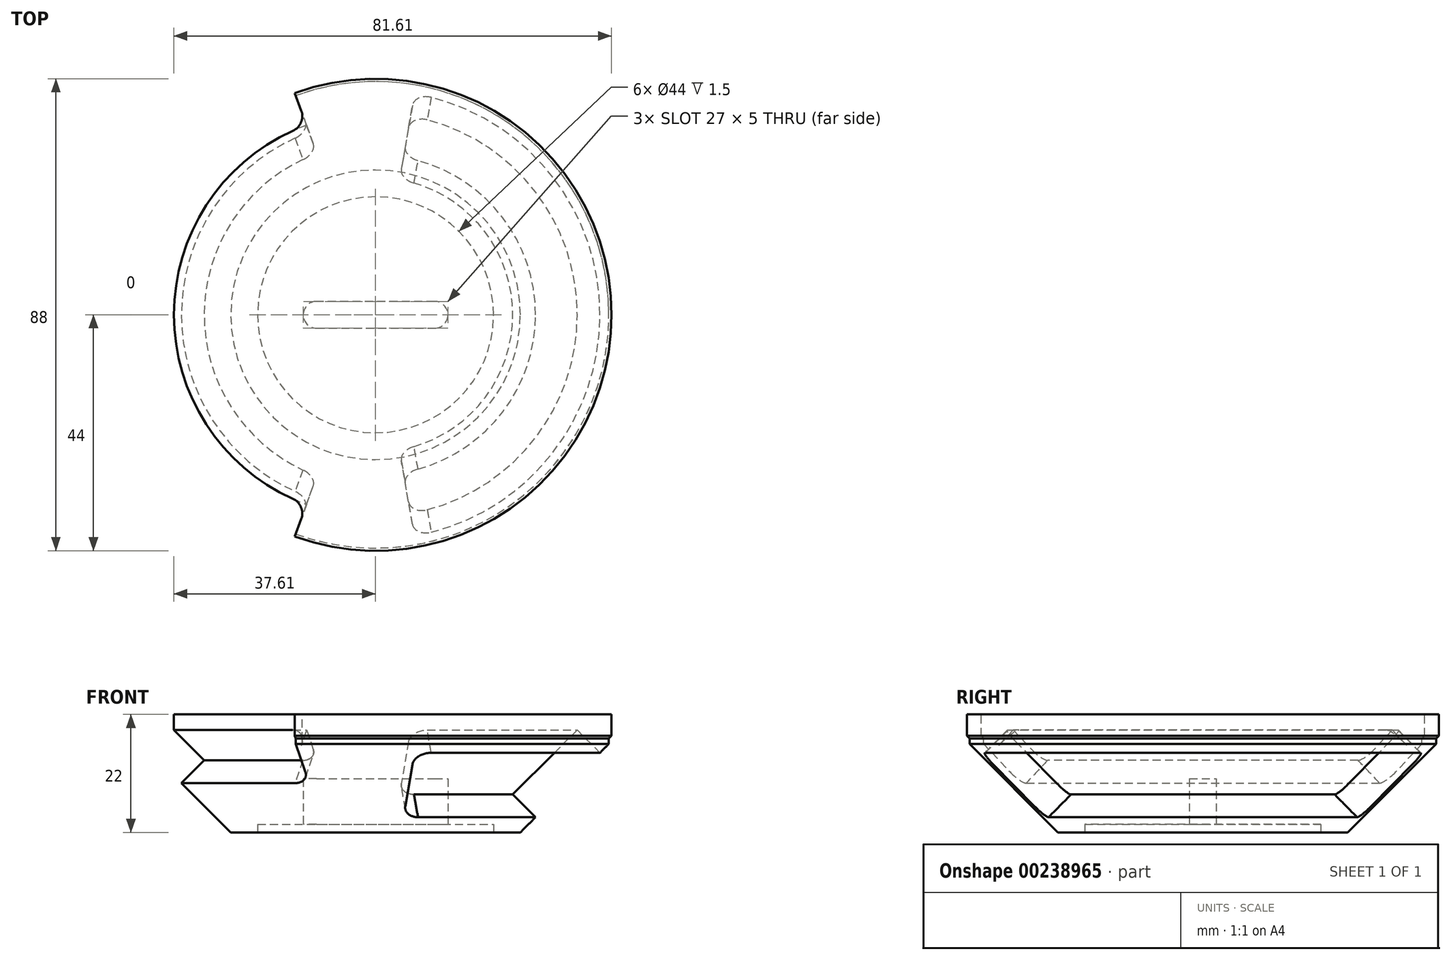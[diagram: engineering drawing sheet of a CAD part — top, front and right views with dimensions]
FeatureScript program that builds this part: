
annotation { "Feature Type Name" : "Feature", "Feature Type Description" : "" }
export const myFeature = defineFeature(function(context is Context, id is Id, definition is map)
    precondition{}
    {
        {
            var Q0;
            Q0=qCreatedBy(makeId("Front.planeOp"),FACE);
            var sketch = newSketch(context, id + "F0", { "sketchPlane" : qUnion([Q0])});
            skLineSegment(sketch, "E0", {"start": v(0, 70.12) * mm, "end": v(0, -51.14) * mm, "construction": true});
            skLineSegment(sketch, "E1", {"start": v(-27, -2) * mm, "end": v(-43.5, 14.5) * mm});
            skLineSegment(sketch, "E2", {"start": v(-44, 20) * mm, "end": v(0, 20) * mm});
            skLineSegment(sketch, "E3", {"start": v(0, 20) * mm, "end": v(0, -2) * mm});
            skLineSegment(sketch, "E4.trimOffspring", {"start": v(-27, -2) * mm, "end": v(0, -2) * mm});
            skLineSegment(sketch, "E5", {"start": v(-47.02, 16) * mm, "end": v(-44, 16) * mm});
            skLineSegment(sketch, "E6", {"start": v(-43.5, 15.5) * mm, "end": v(-43.5, 14.5) * mm});
            skLineSegment(sketch, "E7", {"start": v(-44, 16) * mm, "end": v(-43.5, 15.5) * mm});
            skLineSegment(sketch, "E8.trimOffspring", {"start": v(-44, 16) * mm, "end": v(-44, 20) * mm});
            skPoint(sketch, "E9.orphan", {"position": v(-44, 15) * mm});
            skSolve(sketch);
        }
        {
            var Q0;
            {var subQ0=sQuery(id+"F0.wireOp",EDGE,"E1");Q0=makeQuery(id+"F0.imprint","IMPRINT",FACE,{"disambiguationData":[TD([[makeQuery(id+"F0.imprint","IMPRINT",EDGE,{"derivedFrom":subQ0}),-1.0]])]});}
            var Q1;
            Q1=sQuery(id+"F0.wireOp",EDGE,"E0");
            revolve(context, id + "F1", {"entities" : qUnion([Q0]), "axis" : qUnion([Q1]), "revolveType" : RevolveType.FULL});
        }
        {
            var Q0;
            Q0=qCreatedBy(makeId("Front.planeOp"),FACE);
            var sketch = newSketch(context, id + "F2", { "sketchPlane" : qUnion([Q0])});
            skLineSegment(sketch, "E10", {"start": v(-31.95, 11.44) * mm, "end": v(-41.29, 2.1) * mm});
            skLineSegment(sketch, "E11", {"start": v(-37.6, 17.1) * mm, "end": v(-46.94, 7.75) * mm});
            skLineSegment(sketch, "E12", {"start": v(-37.6, 17.1) * mm, "end": v(-31.95, 11.44) * mm});
            skLineSegment(sketch, "E13", {"start": v(-46.94, 7.75) * mm, "end": v(-41.29, 2.1) * mm});
            skSolve(sketch);
        }
        {
            var Q0;
            Q0=qCreatedBy(makeId("Front.planeOp"),FACE);
            var sketch = newSketch(context, id + "F3", { "sketchPlane" : qUnion([Q0])});
            skLineSegment(sketch, "E14.0", {"start": v(-37.6, 8.6) * mm, "end": v(-37.6, 25) * mm});
            skLineSegment(sketch, "E15.0", {"start": v(-27, -2) * mm, "end": v(-43.5, 14.5) * mm, "construction": true});
            skLineSegment(sketch, "E16", {"start": v(-46, 25) * mm, "end": v(-46, 8.6) * mm});
            skLineSegment(sketch, "E17", {"start": v(-37.6, 8.6) * mm, "end": v(-46, 8.6) * mm});
            skLineSegment(sketch, "E18.0", {"start": v(-44, 20) * mm, "end": v(0, 20) * mm, "construction": true});
            skLineSegment(sketch, "E19", {"start": v(-37.6, 25) * mm, "end": v(-46, 25) * mm});
            skSolve(sketch);
        }
        {
            var Q0;
            Q0=qSketchRegion(id+"F3",true);
            var Q1;
            Q1=sQuery(id+"F0.wireOp",EDGE,"E0");
            revolve(context, id + "F4", {"entities" : qUnion([Q0]), "axis" : qUnion([Q1]), "revolveType" : RevolveType.TWO_DIRECTIONS, "angle" : 70 * degree, "angleBack" : 290 * degree});
        }
        {
            var Q0;
            Q0=qCreatedBy(makeId("Front.planeOp"),FACE);
            var sketch = newSketch(context, id + "F5", { "sketchPlane" : qUnion([Q0])});
            skLineSegment(sketch, "E20", {"start": v(-25.59, 5.07) * mm, "end": v(-36.9, -6.24) * mm});
            skLineSegment(sketch, "E21", {"start": v(-37.6, 17.1) * mm, "end": v(-48.92, 5.78) * mm});
            skLineSegment(sketch, "E22", {"start": v(-37.6, 17.1) * mm, "end": v(-25.59, 5.07) * mm});
            skLineSegment(sketch, "E23", {"start": v(-48.92, 5.78) * mm, "end": v(-36.9, -6.24) * mm});
            skSolve(sketch);
        }
        {
            var Q0;
            Q0=qSketchRegion(id+"F5",true);
            var Q1;
            Q1=sQuery(id+"F0.wireOp",EDGE,"E3");
            revolve(context, id + "F6", {"entities" : qUnion([Q0]), "axis" : qUnion([Q1]), "revolveType" : RevolveType.TWO_DIRECTIONS, "angle" : 260 * degree, "angleBack" : 100 * degree});
        }
        {
            var Q0;
            Q0=qSketchRegion(id+"F2",true);
            var Q1;
            Q1=sQuery(id+"F0.wireOp",EDGE,"E3");
            revolve(context, id + "F7", {"entities" : qUnion([Q0]), "axis" : qUnion([Q1]), "revolveType" : RevolveType.TWO_DIRECTIONS, "angle" : 70 * degree, "angleBack" : 290 * degree});
        }
        {
            var Q0;
            Q0=makeQuery(id+"F7.opRevolve","CAP_EDGE",EDGE,{"disambiguationData":[OSD([sQuery(id+"F2.wireOp",EDGE,"E10")])],"isStart":true});
            var Q1;
            Q1=makeQuery(id+"F7.opRevolve","CAP_EDGE",EDGE,{"disambiguationData":[OSD([sQuery(id+"F2.wireOp",EDGE,"E10")])],"isStart":false});
            var Q2;
            Q2=makeQuery(id+"F4.opRevolve","CAP_EDGE",EDGE,{"disambiguationData":[OSD([sQuery(id+"F3.wireOp",EDGE,"E14.0")])],"isStart":false});
            var Q3;
            Q3=makeQuery(id+"F4.opRevolve","CAP_EDGE",EDGE,{"disambiguationData":[OSD([sQuery(id+"F3.wireOp",EDGE,"E14.0")])],"isStart":true});
            fillet(context, id + "F8", {"entities" : qUnion([Q0, Q1, Q2, Q3]), "radius" : 3 * mm, "tangentPropagation" : true, "allowEdgeOverflow" : false});
        }
        {
            var Q0;
            Q0=makeQuery(id+"F6.opRevolve","CAP_EDGE",EDGE,{"disambiguationData":[OSD([sQuery(id+"F5.wireOp",EDGE,"E20")])],"isStart":true});
            var Q1;
            Q1=makeQuery(id+"F6.opRevolve","CAP_EDGE",EDGE,{"disambiguationData":[OSD([sQuery(id+"F5.wireOp",EDGE,"E21")])],"isStart":true});
            var Q2;
            Q2=makeQuery(id+"F6.opRevolve","CAP_EDGE",EDGE,{"disambiguationData":[OSD([sQuery(id+"F5.wireOp",EDGE,"E21")])],"isStart":false});
            var Q3;
            Q3=makeQuery(id+"F6.opRevolve","CAP_EDGE",EDGE,{"disambiguationData":[OSD([sQuery(id+"F5.wireOp",EDGE,"E20")])],"isStart":false});
            fillet(context, id + "F9", {"entities" : qUnion([Q0, Q1, Q2, Q3]), "radius" : 3 * mm, "tangentPropagation" : true, "allowEdgeOverflow" : false});
        }
        {
            var Q0;
            Q0=makeQuery(id+"F7.opRevolve","SWEPT_BODY",BODY,{"disambiguationData":[OSD([sQuery(id+"F2.wireOp",EDGE,"E10"),sQuery(id+"F2.wireOp",EDGE,"E11"),sQuery(id+"F2.wireOp",EDGE,"E12"),sQuery(id+"F2.wireOp",EDGE,"E13")])]});
            var Q1;
            Q1=makeQuery(id+"F4.opRevolve","SWEPT_BODY",BODY,{"disambiguationData":[OSD([sQuery(id+"F3.wireOp",EDGE,"E14.0"),sQuery(id+"F3.wireOp",EDGE,"E16"),sQuery(id+"F3.wireOp",EDGE,"E17"),sQuery(id+"F3.wireOp",EDGE,"E19")])]});
            var Q2;
            Q2=makeQuery(id+"F6.opRevolve","SWEPT_BODY",BODY,{"disambiguationData":[OSD([sQuery(id+"F5.wireOp",EDGE,"E20"),sQuery(id+"F5.wireOp",EDGE,"E21"),sQuery(id+"F5.wireOp",EDGE,"E22"),sQuery(id+"F5.wireOp",EDGE,"E23")])]});
            var Q3;
            Q3=makeQuery(id+"F1.opRevolve","SWEPT_BODY",BODY,{"disambiguationData":[OSD([sQuery(id+"F0.wireOp",EDGE,"E1"),sQuery(id+"F0.wireOp",EDGE,"E2"),sQuery(id+"F0.wireOp",EDGE,"f3fcd404-e105-45fe-9513-618a2d7f6fcb.trimOffspring"),sQuery(id+"F0.wireOp",EDGE,"E3"),sQuery(id+"F0.wireOp",EDGE,"E4.trimOffspring")])]});
            booleanBodies(context, id + "F10", {"operationType" : BooleanOperationType.SUBTRACTION, "tools" : qUnion([Q0, Q1, Q2]), "targets" : qUnion([Q3])});
        }
        {
            var Q0;
            Q0=makeQuery(id+"F1.opRevolve","SWEPT_FACE",FACE,{"disambiguationData":[OSD([sQuery(id+"F0.wireOp",EDGE,"E4.trimOffspring")])]});
            cPlane(context, id + "F11", {"entities" : qUnion([Q0]), "cplaneType" : CPlaneType.OFFSET, "offset" : 0 * mm, "width" : 150 * mm, "height" : 150 * mm});
        }
        {
            var Q0;
            Q0=qCreatedBy(id+"F11.planeOp",FACE);
            var sketch = newSketch(context, id + "F12", { "sketchPlane" : qUnion([Q0])});
            skCircle(sketch, "E24.0", {"center": v(0, 0) * mm, "radius": 27 * mm, "construction": true});
            skLineSegment(sketch, "E25", {"start": v(-11, -2.5) * mm, "end": v(0, -2.5) * mm});
            skCircle(sketch, "E26", {"center": v(0, 1.34) * mm, "radius": 10 * mm, "construction": true});
            skLineSegment(sketch, "E27", {"start": v(-43.6, 0) * mm, "end": v(51.09, 0) * mm, "construction": true});
            skLineSegment(sketch, "E28", {"start": v(0, -52.24) * mm, "end": v(0, 58.72) * mm, "construction": true});
            skLineSegment(sketch, "E29.MirrorCS", {"start": v(-11, 2.5) * mm, "end": v(0, 2.5) * mm});
            skArc(sketch, "E30.trimOffspring", {"start": v(-11, 2.5) * mm, "mid": v(-13.5, 0) * mm, "end": v(-11, -2.5) * mm});
            skArc(sketch, "E31.MirrorCS", {"start": v(11, 2.5) * mm, "mid": v(13.5, 0) * mm, "end": v(11, -2.5) * mm});
            skLineSegment(sketch, "E32.MirrorCS", {"start": v(11, -2.5) * mm, "end": v(0, -2.5) * mm});
            skLineSegment(sketch, "E33.MirrorCS", {"start": v(11, 2.5) * mm, "end": v(0, 2.5) * mm});
            skCircle(sketch, "E34", {"center": v(0, 0) * mm, "radius": 13.5 * mm, "construction": true});
            skSolve(sketch);
        }
        {
            var Q0;
            Q0=qSketchRegion(id+"F12",true);
            extrude(context, id + "F13", {"entities" : qUnion([Q0]), "operationType" : NewBodyOperationType.REMOVE, "oppositeDirection" : true, "depth" : 10 * mm});
        }
        {
            var Q0;
            Q0=qCreatedBy(id+"F11.planeOp",FACE);
            var sketch = newSketch(context, id + "F14", { "sketchPlane" : qUnion([Q0])});
            skCircle(sketch, "E35", {"center": v(0, 0) * mm, "radius": 22 * mm});
            skCircle(sketch, "E36", {"center": v(0, 0) * mm, "radius": 15 * mm, "construction": true});
            skSolve(sketch);
        }
        {
            var Q0;
            Q0=qSketchRegion(id+"F14",true);
            extrude(context, id + "F15", {"entities" : qUnion([Q0]), "operationType" : NewBodyOperationType.REMOVE, "oppositeDirection" : true, "depth" : 1.5 * mm});
        }
    });
